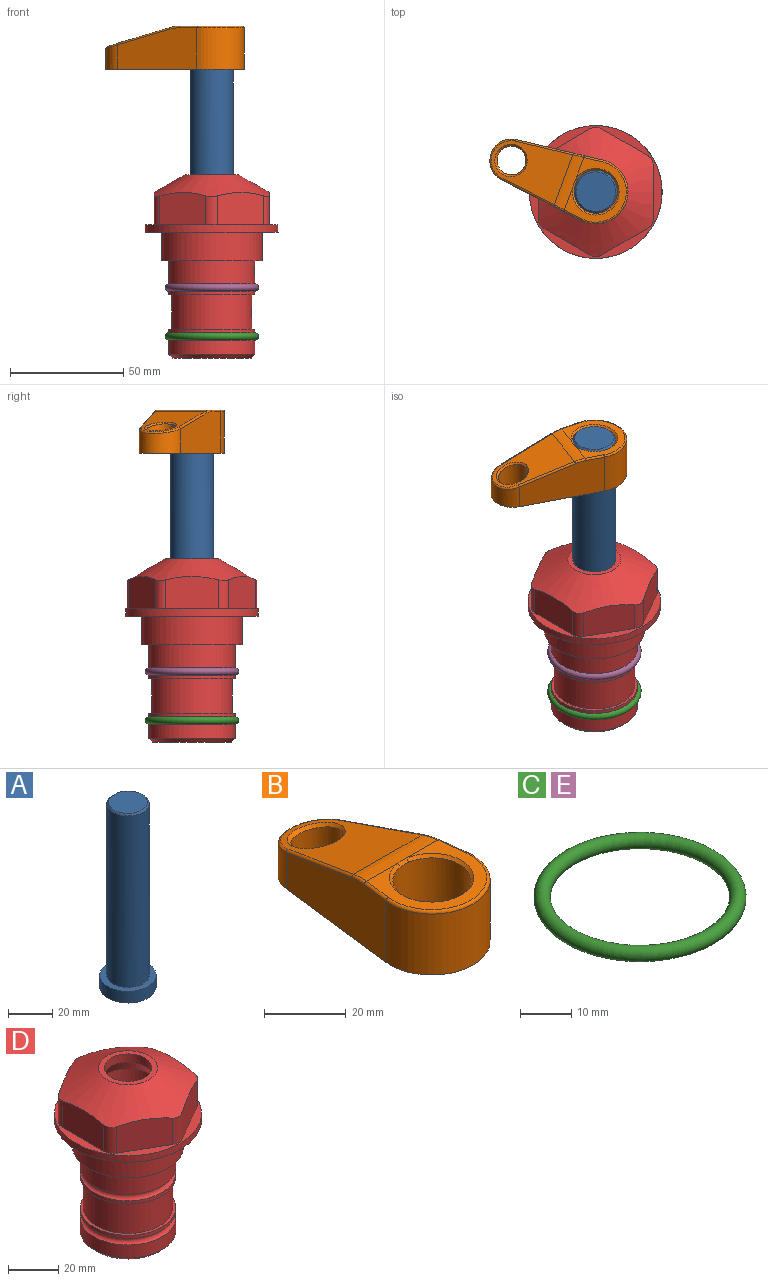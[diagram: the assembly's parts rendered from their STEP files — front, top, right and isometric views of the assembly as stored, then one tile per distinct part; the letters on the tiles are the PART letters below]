
ASSEMBLY  parts=5 mates=4
PART A: 6 faces, bbox 25.4x25.4x101.6 mm
  f0: plane 17.46x17.46mm, normal (0,0,1), area 239.5mm2, adj f5
  f1: plane 25.4x25.4mm, normal (0,0,-1), area 506.7mm2, adj f2
  f2: cylinder r=12.7mm len=25.4mm, axis (0,0,1), area 506.7mm2, adj f1,f3
  f3: plane 25.4x25.4mm, normal (0,0,1), area 221.7mm2, adj f2,f4
  f4: cylinder r=9.53mm len=94.46mm, axis (0,0,1), area 5653mm2, adj f3,f5
  f5: cone r=8.73mm half-angle=45deg, axis (0,0,-1), area 64.4mm2, adj f0,f4
PART B: 31 faces, bbox 31.7x65.5x19.8 mm
  f0: plane 39.12x18.26mm, normal (0.99,0.12,0), area 612.2mm2, adj f1,f4,f7,f11,f13,f15
  f1: cylinder r=9.53mm len=18.91mm, axis (0,0,-1), area 296.1mm2, adj f0,f2,f7,f17
  f2: plane 39.12x18.26mm, normal (-0.99,0.12,0), area 612.2mm2, adj f1,f4,f7,f12,f14,f16
  f3: cylinder r=6.35mm len=12.7mm, axis (0,0,-1), area 362.4mm2, adj f7,f18
  f4: cylinder r=14.29mm len=28.58mm, axis (0,0,-1), area 882.2mm2, adj f0,f2,f7,f10
  f5: cylinder r=9.53mm len=19.05mm, axis (0,0,-1), area 1092.6mm2, adj f7,f19,f20
  f6: plane 26.99x23.69mm, normal (0,0,1), area 216.2mm2, adj f9,f10,f11,f12,f19
  f7: plane 63.5x28.58mm, normal (0,0,-1), area 661.8mm2, adj f0,f1,f2,f3,f4,f5,f22,f23
  f8: plane 33.52x23.6mm, normal (0,0.26,0.97), area 486mm2, adj f9,f15,f16,f17,f18
  f9: cylinder r=19.05mm len=24.72mm, axis (1,0,0), area 120.4mm2, adj f6,f8,f13,f14,f20
  f10: torus R=13.49mm, axis (0,0,1), area 59mm2, adj f4,f6,f11,f12
  f11: cylinder r=0.79mm len=8.67mm, axis (0.12,-0.99,0), area 10.8mm2, adj f0,f6,f10,f13
  f12: cylinder r=0.79mm len=8.67mm, axis (0.12,0.99,0), area 10.8mm2, adj f2,f6,f10,f14
  f13: bspline ~4.95x1.42mm, area 6.1mm2, adj f0,f9,f11,f15
  f14: bspline ~4.95x1.42mm, area 6.1mm2, adj f2,f9,f12,f16
  f15: cylinder r=0.79mm len=25.95mm, axis (0.12,-0.96,0.26), area 32.9mm2, adj f0,f8,f13,f17
  f16: cylinder r=0.79mm len=25.95mm, axis (0.12,0.96,-0.26), area 32.9mm2, adj f2,f8,f14,f17
  f17: bspline ~18.91x8.38mm, area 30mm2, adj f1,f8,f15,f16
  f18: bspline ~14.29x14.29mm, area 48.3mm2, adj f3,f8
  f19: cone r=9.53mm half-angle=45deg, axis (0,0,1), area 66.5mm2, adj f5,f6,f20
  f20: bspline ~3.22x0.96mm, area 3.5mm2, adj f5,f9,f19
  f21: plane 2.75x2.72mm, normal (0,0,-1), area 2.9mm2, adj f23,f25,f28
  f22: plane 23.05x15.88mm, normal (-0.99,-0.12,0), area 323.6mm2, adj f7,f25,f26,f27,f28,f29
  f23: plane 23.05x15.88mm, normal (0.99,-0.12,0), area 323.6mm2, adj f7,f21,f25,f27,f28,f30
  f24: cylinder r=9.53mm len=10.69mm, axis (0,0,-1), area 114.7mm2, adj f7,f27,f29,f30
  f25: cylinder r=12.7mm len=20.59mm, axis (0,0,-1), area 381.1mm2, adj f7,f21,f22,f23,f26,f28
  f26: plane 2.75x2.72mm, normal (0,0,-1), area 2.9mm2, adj f22,f25,f28
  f27: plane 19.72x18.37mm, normal (0,-0.26,-0.97), area 291.8mm2, adj f22,f23,f24,f28,f29,f30
  f28: cylinder r=15.88mm len=19.92mm, axis (1,0,0), area 54.8mm2, adj f21,f22,f23,f25,f26,f27
  f29: cylinder r=1.59mm len=11mm, axis (0,0,-1), area 34.7mm2, adj f7,f22,f24,f27
  f30: cylinder r=1.59mm len=11mm, axis (0,0,-1), area 34.7mm2, adj f7,f23,f24,f27
PART C: 1 faces, bbox 44.7x44.7x3.2 mm
  f0: torus R=19.05mm, axis (0,0,1), area 1193.9mm2
PART D: 36 faces, bbox 58.7x58.7x81 mm
  f0: cylinder r=17.78mm len=35.56mm, axis (0,0,1), area 1670.8mm2, adj f23,f24,f31
  f1: cylinder r=19.05mm len=38.1mm, axis (0,0,1), area 1191.9mm2, adj f26,f27,f30
  f2: plane 58.66x58.66mm, normal (0,0,-1), area 1150.6mm2, adj f3,f28
  f3: cylinder r=29.33mm len=58.66mm, axis (0,0,-1), area 585.1mm2, adj f2,f4
  f4: plane 58.66x58.66mm, normal (0,0,1), area 475.9mm2, adj f3,f5,f6,f7,f8,f9,f10,f11
  f5: plane 20.32x14.34mm, normal (-0.5,0.87,0), area 324.4mm2, adj f4,f15,f16,f17
  f6: plane 20.32x14.34mm, normal (0.5,0.87,0), area 324.4mm2, adj f4,f14,f15,f17
  f7: plane 23.48x14.34mm, normal (1,0,0), area 324.4mm2, adj f4,f13,f14,f17
  f8: plane 20.32x14.34mm, normal (0.5,-0.87,0), area 324.4mm2, adj f4,f12,f13,f17
  f9: plane 20.32x14.34mm, normal (-0.5,-0.87,0), area 324.4mm2, adj f4,f11,f12,f17
  f10: plane 23.48x14.34mm, normal (-1,0,0), area 324.4mm2, adj f4,f11,f16,f17
  f11: cylinder r=5.08mm len=12.85mm, axis (0,0,-1), area 67.2mm2, adj f4,f9,f10,f17
  f12: cylinder r=5.08mm len=12.85mm, axis (0,0,-1), area 67.2mm2, adj f4,f8,f9,f17
  f13: cylinder r=5.08mm len=12.85mm, axis (0,0,-1), area 67.2mm2, adj f4,f7,f8,f17
  f14: cylinder r=5.08mm len=12.85mm, axis (0,0,-1), area 67.2mm2, adj f4,f6,f7,f17
  f15: cylinder r=5.08mm len=12.85mm, axis (0,0,-1), area 67.2mm2, adj f4,f5,f6,f17
  f16: cylinder r=5.08mm len=12.85mm, axis (0,0,-1), area 67.2mm2, adj f4,f5,f10,f17
  f17: cone r=11.73mm half-angle=60deg, axis (0,0,-1), area 2071.8mm2, adj f5,f6,f7,f8,f9,f10,f11,f12
  f18: plane 23.46x23.46mm, normal (0,0,1), area 147.4mm2, adj f17,f35
  f19: plane 34.93x34.93mm, normal (0,0,-1), area 958mm2, adj f29
  f20: cylinder r=19.05mm len=38.1mm, axis (0,0,1), area 760.1mm2, adj f21,f29
  f21: torus R=19.05mm, axis (0,0,1), area 565.3mm2, adj f20,f22
  f22: cylinder r=19.05mm len=38.1mm, axis (0,0,1), area 190mm2, adj f21,f23
  f23: plane 38.1x38.1mm, normal (0,0,1), area 146.9mm2, adj f0,f22
  f24: plane 38.1x38.1mm, normal (0,0,-1), area 146.9mm2, adj f0,f25
  f25: cylinder r=19.05mm len=38.1mm, axis (0,0,1), area 190mm2, adj f24,f26
  f26: torus R=19.05mm, axis (0,0,1), area 565.3mm2, adj f1,f25
  f27: plane 44.45x44.45mm, normal (0,0,-1), area 411.7mm2, adj f1,f28
  f28: cylinder r=22.23mm len=44.45mm, axis (0,0,1), area 1773.5mm2, adj f2,f27
  f29: cone r=19.05mm half-angle=45deg, axis (0,0,1), area 257.5mm2, adj f19,f20
  f30: cylinder r=3.17mm len=6.75mm, axis (-1,0,0), area 128mm2, adj f1,f33
  f31: cylinder r=3.17mm len=6.35mm, axis (-1,0,0), area 102.5mm2, adj f0,f33
  f32: plane 25.4x25.4mm, normal (0,0,1), area 506.7mm2, adj f33
  f33: cylinder r=12.7mm len=66.42mm, axis (0,0,-1), area 5236.2mm2, adj f30,f31,f32,f34
  f34: cone r=9.53mm half-angle=30deg, axis (0,0,-1), area 443.4mm2, adj f33,f35
  f35: cylinder r=9.53mm len=19.05mm, axis (0,0,-1), area 240.9mm2, adj f18,f34
PART E: same geometry as C
PLACE A t=(0,0,27.55)mm
PLACE B rot(axis=(0,0,1),69.7deg) t=(0,0,27.55)mm
PLACE C t=(0,0,-21.59)mm
PLACE D at identity fixed
PLACE E at identity
MATE cylindrical A.f2 <-> D.f0  axis (0,0,-1) through (0,0,-10.55)mm
MATE fastened C.f0 <-> D.f0  axis (0,0,1) through (0,0,-46.1)mm
MATE revolute A.f2 <-> B.f4  axis (0,0,1) through (0,0,91.05)mm
MATE fastened E.f0 <-> D.f0  axis (0,0,1) through (0,0,-24.51)mm
